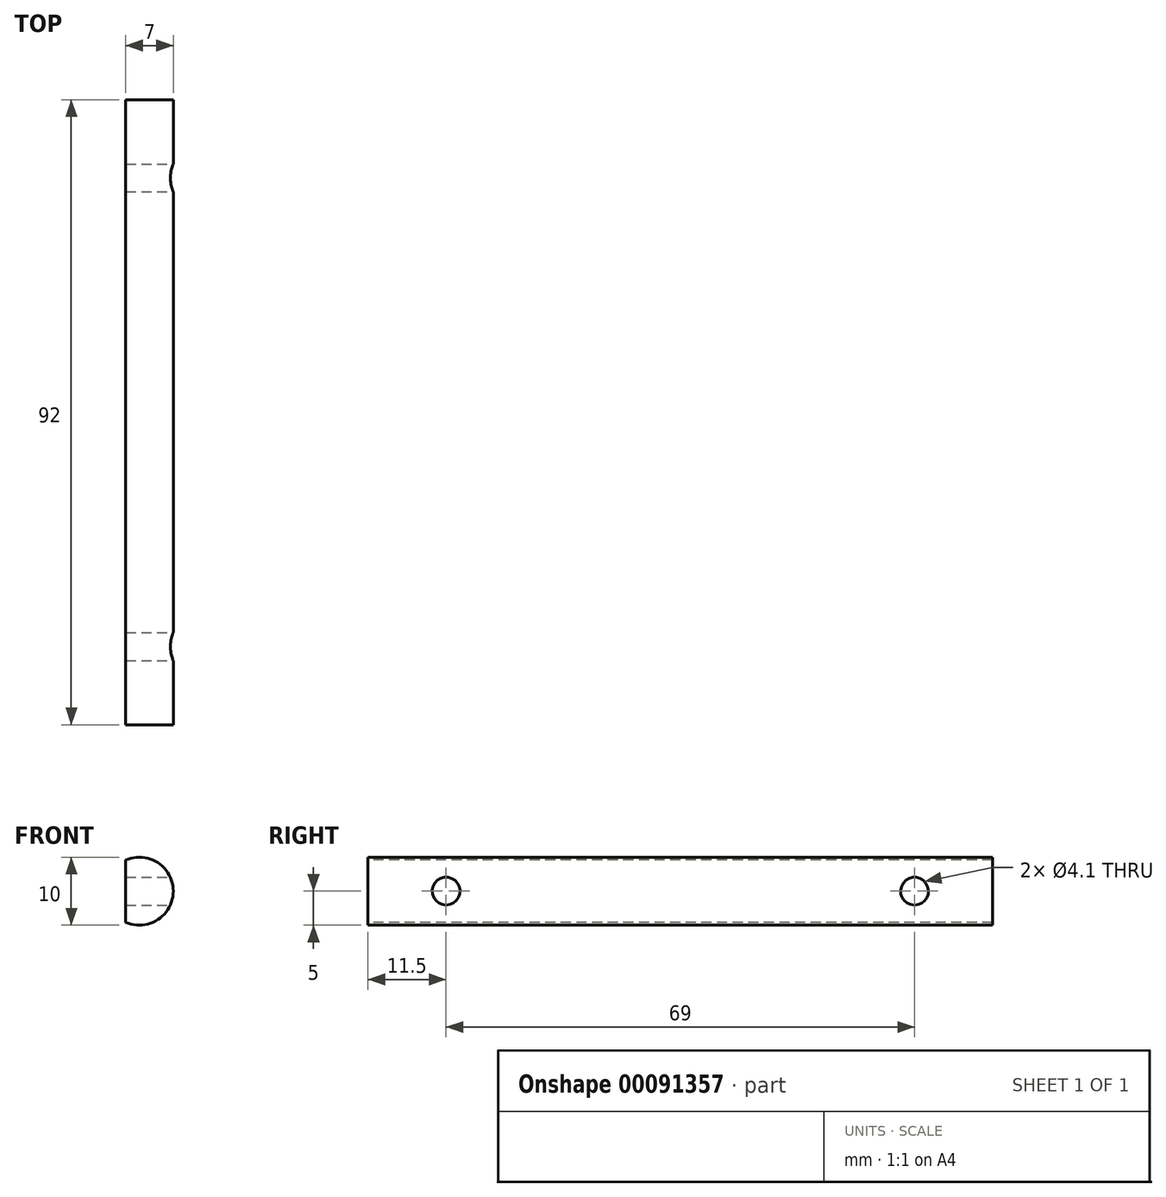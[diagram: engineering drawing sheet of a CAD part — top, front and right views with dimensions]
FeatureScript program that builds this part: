
annotation { "Feature Type Name" : "Feature", "Feature Type Description" : "" }
export const myFeature = defineFeature(function(context is Context, id is Id, definition is map)
    precondition{}
    {
        {
            var Q0;
            Q0=qCreatedBy(makeId("Front.planeOp"),FACE);
            var sketch = newSketch(context, id + "F0", { "sketchPlane" : qUnion([Q0])});
            skArc(sketch, "E0", {"start": v(-2, -4.58) * mm, "mid": v(5, 0) * mm, "end": v(-2, 4.58) * mm});
            skLineSegment(sketch, "E1", {"start": v(0, 19.83) * mm, "end": v(0, -19.5) * mm, "construction": true});
            skLineSegment(sketch, "E2", {"start": v(-2, 4.58) * mm, "end": v(-2, -4.58) * mm});
            skSolve(sketch);
        }
        {
            var Q0;
            Q0=makeQuery(id+"F0.imprint","IMPRINT",FACE,{"disambiguationData":[TD([[makeQuery(id+"F0.imprint","IMPRINT",EDGE,{"derivedFrom":sQuery(id+"F0.wireOp",EDGE,"E0")}),1.0]])]});
            extrude(context, id + "F1", {"entities" : qUnion([Q0]), "oppositeDirection" : true, "depth" : 92 * mm});
        }
        {
            var Q0;
            Q0=makeQuery(id+"F1.opExtrude","SWEPT_FACE",FACE,{"disambiguationData":[OSD([sQuery(id+"F0.wireOp",EDGE,"E2")])]});
            var sketch = newSketch(context, id + "F2", { "sketchPlane" : qUnion([Q0])});
            skLineSegment(sketch, "E3", {"start": v(0, 0) * mm, "end": v(-92, 0) * mm, "construction": true});
            skPoint(sketch, "E4", {"position": v(-80.5, 0) * mm});
            skPoint(sketch, "E5", {"position": v(-11.5, 0) * mm});
            skSolve(sketch);
        }
        {
            var Q0;
            Q0=sQuery(id+"F2.wireOp",VERTEX,"E4");
            var Q1;
            Q1=sQuery(id+"F2.wireOp",VERTEX,"E5");
            var Q2;
            Q2=makeQuery(id+"F1.opExtrude","SWEPT_BODY",BODY,{"disambiguationData":[OSD([sQuery(id+"F0.wireOp",EDGE,"E0"),sQuery(id+"F0.wireOp",EDGE,"E2")])]});
            hole(context, id + "F3", {"style" : HoleStyle.SIMPLE, "endStyle" : HoleEndStyle.THROUGH, "standardTappedOrClearance" : lookupTablePath({ "standard" : "ISO", "engagement" : "75%", "pitch" : "0.9 mm", "size" : "M5", "type" : "Tapped" }), "standardBlindInLast" : lookupTablePath({ "standard" : "ISO", "engagement" : "75%", "pitch" : "0.9 mm", "size" : "M5", "type" : "Tapped" }), "holeDiameter" : 4.1 * mm, "locations" : qUnion([Q0, Q1]), "scope" : qUnion([Q2]), "isTappedThrough" : true, "showTappedDepth" : true, "startStyle" : HoleStartStyle.SKETCH});
        }
    });
